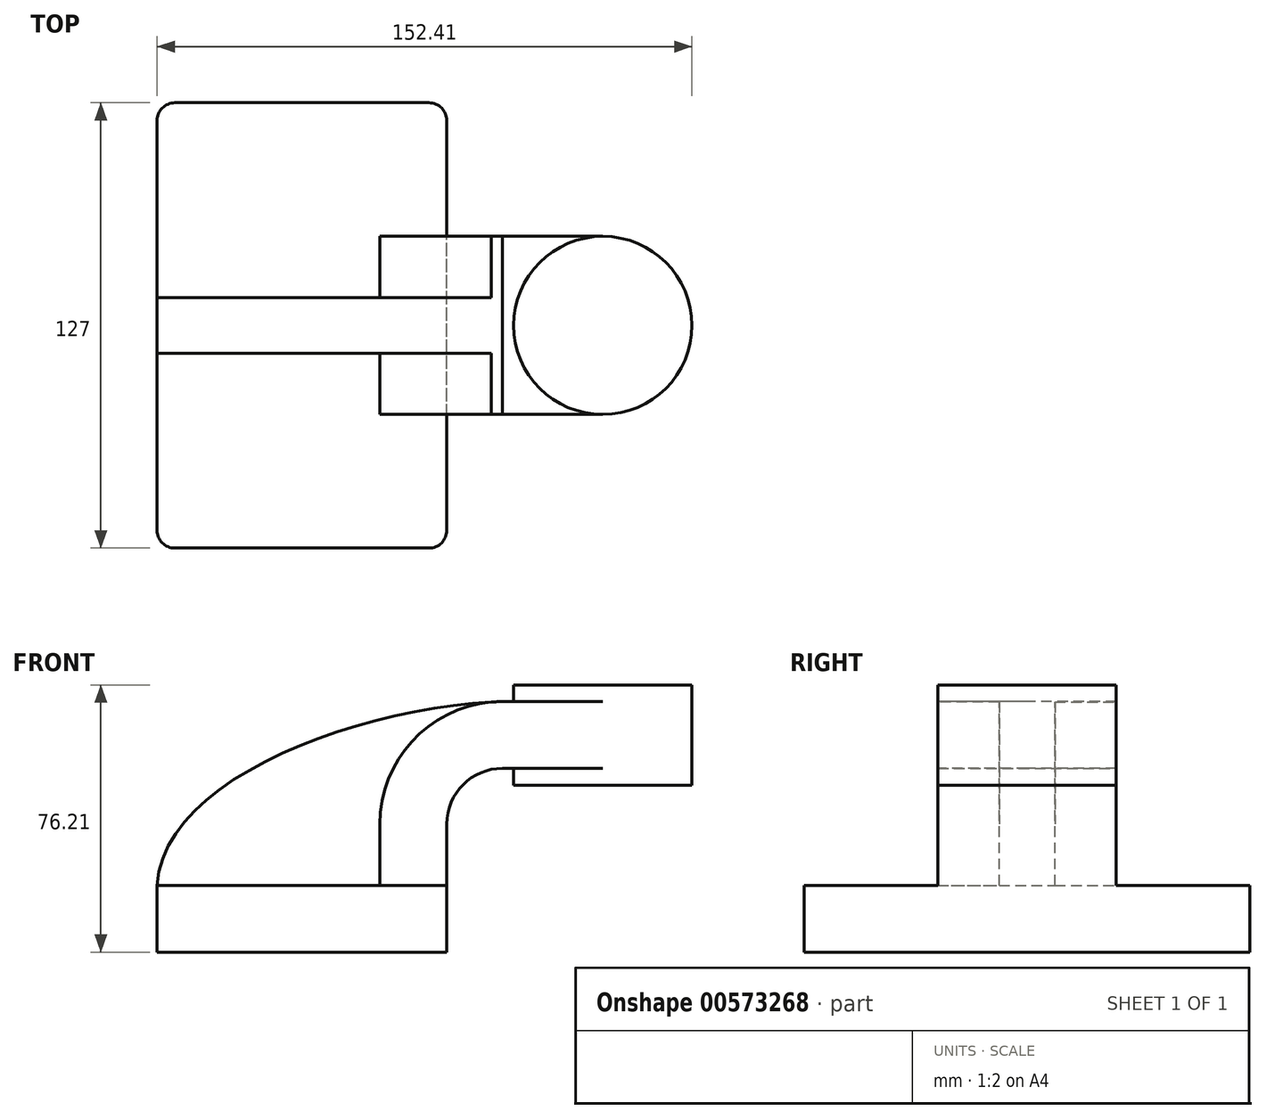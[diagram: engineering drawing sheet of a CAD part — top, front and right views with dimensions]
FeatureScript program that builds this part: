
annotation { "Feature Type Name" : "Feature", "Feature Type Description" : "" }
export const myFeature = defineFeature(function(context is Context, id is Id, definition is map)
    precondition{}
    {
        {
            var Q0;
            Q0=qCreatedBy(makeId("Front.planeOp"),FACE);
            var sketch = newSketch(context, id + "F0", { "sketchPlane" : qUnion([Q0])});
            skLineSegment(sketch, "E0.rect.bottom", {"start": v(-41.28, 9.52) * mm, "end": v(41.28, 9.52) * mm});
            skLineSegment(sketch, "E0.rect.top", {"start": v(-41.28, -9.52) * mm, "end": v(41.28, -9.52) * mm});
            skLineSegment(sketch, "E0.rect.left", {"start": v(-41.28, 9.52) * mm, "end": v(-41.28, -9.52) * mm});
            skLineSegment(sketch, "E0.rect.right", {"start": v(41.28, 9.52) * mm, "end": v(41.28, -9.52) * mm});
            skPoint(sketch, "E0.rect.middle", {"position": v(0, 0) * mm});
            skLineSegment(sketch, "E1", {"start": v(41.28, 9.52) * mm, "end": v(41.28, 27) * mm});
            skArc(sketch, "E2", {"start": v(41.28, 27) * mm, "mid": v(45.92, 38.23) * mm, "end": v(57.15, 42.88) * mm});
            skLineSegment(sketch, "E3", {"start": v(57.15, 42.88) * mm, "end": v(85.72, 42.88) * mm});
            skLineSegment(sketch, "E4.rect.bottom", {"start": v(60.32, 38.1) * mm, "end": v(111.12, 38.1) * mm});
            skLineSegment(sketch, "E4.rect.top", {"start": v(60.32, 66.68) * mm, "end": v(111.12, 66.68) * mm});
            skLineSegment(sketch, "E4.rect.left", {"start": v(60.32, 38.1) * mm, "end": v(60.32, 66.68) * mm});
            skLineSegment(sketch, "E4.rect.right", {"start": v(111.13, 38.1) * mm, "end": v(111.12, 66.68) * mm});
            skPoint(sketch, "E4.rect.middle", {"position": v(85.72, 52.39) * mm});
            skLineSegment(sketch, "E5.0", {"start": v(57.15, 61.93) * mm, "end": v(85.72, 61.93) * mm});
            skArc(sketch, "E5.1", {"start": v(22.23, 27) * mm, "mid": v(32.45, 51.7) * mm, "end": v(57.15, 61.93) * mm});
            skLineSegment(sketch, "E5.2", {"start": v(22.23, 9.52) * mm, "end": v(22.23, 27) * mm});
            skLineSegment(sketch, "E6", {"start": v(85.72, 38.1) * mm, "end": v(85.72, 66.68) * mm});
            skFitSpline(sketch, "E7", {"points": [v(-41.28, 9.53) * mm, v(57.15, 61.93) * mm], "startDerivative": vector(5.2, 92.34) * mm, "endDerivative": vector(120.92, 4.22) * mm});
            skSolve(sketch);
        }
        {
            var Q0;
            Q0=makeQuery(id+"F0.imprint","IMPRINT",FACE,{"disambiguationData":[TD([[makeQuery(id+"F0.imprint","IMPRINT",EDGE,{"derivedFrom":sQuery(id+"F0.wireOp",EDGE,"E0.rect.top")}),1.0]])]});
            extrude(context, id + "F1", {"entities" : qUnion([Q0]), "endBound" : BoundingType.SYMMETRIC, "depth" : 127 * mm});
        }
        {
            var Q0;
            {var subQ9=sQuery(id+"F0.wireOp",EDGE,"E1");Q0=makeQuery(id+"F0.imprint","IMPRINT",FACE,{"disambiguationData":[TD([[makeQuery(id+"F0.imprint","IMPRINT",EDGE,{"derivedFrom":subQ9}),1.0]])]});}
            var Q1;
            {var subQ0=sQuery(id+"F0.wireOp",EDGE,"E6");var subQ1=sQuery(id+"F0.wireOp",EDGE,"E3");var subQ2=makeQuery(id+"F0.imprint","INTERSECT",VERTEX,{"derivedFrom":[subQ1,subQ0]});Q1=makeQuery(id+"F0.imprint","IMPRINT",FACE,{"disambiguationData":[TD([[makeQuery(id+"F0.imprint","IMPRINT",EDGE,{"disambiguationData":[TD([[subQ2,1.0]])],"derivedFrom":subQ1}),1.0]])]});}
            extrude(context, id + "F2", {"entities" : qUnion([Q0, Q1]), "operationType" : NewBodyOperationType.ADD, "endBound" : BoundingType.SYMMETRIC, "depth" : 50.8 * mm});
        }
        {
            var Q0;
            {var subQ3=sQuery(id+"F0.wireOp",EDGE,"E5.2");Q0=makeQuery(id+"F0.imprint","IMPRINT",FACE,{"disambiguationData":[TD([[makeQuery(id+"F0.imprint","IMPRINT",EDGE,{"derivedFrom":subQ3}),1.0]])]});}
            extrude(context, id + "F3", {"entities" : qUnion([Q0]), "operationType" : NewBodyOperationType.ADD, "endBound" : BoundingType.SYMMETRIC, "depth" : 15.88 * mm});
        }
        {
            var Q0;
            {var subQ5=sQuery(id+"F0.wireOp",EDGE,"E4.rect.right");Q0=makeQuery(id+"F0.imprint","IMPRINT",FACE,{"disambiguationData":[TD([[makeQuery(id+"F0.imprint","IMPRINT",EDGE,{"derivedFrom":subQ5}),1.0]])]});}
            var Q1;
            Q1=sQuery(id+"F0.wireOp",EDGE,"E6");
            revolve(context, id + "F4", {"operationType" : NewBodyOperationType.ADD, "entities" : qUnion([Q0]), "axis" : qUnion([Q1]), "revolveType" : RevolveType.FULL});
        }
        {
            var Q0;
            Q0=makeQuery(id+"F1.opExtrude","CAP_EDGE",EDGE,{"disambiguationData":[OSD([sQuery(id+"F0.wireOp",EDGE,"E0.rect.right")])],"isStart":false});
            var Q1;
            Q1=makeQuery(id+"F1.opExtrude","CAP_EDGE",EDGE,{"disambiguationData":[OSD([sQuery(id+"F0.wireOp",EDGE,"E0.rect.left")])],"isStart":false});
            var Q2;
            Q2=makeQuery(id+"F1.opExtrude","CAP_EDGE",EDGE,{"disambiguationData":[OSD([sQuery(id+"F0.wireOp",EDGE,"E0.rect.right")])],"isStart":true});
            var Q3;
            Q3=makeQuery(id+"F1.opExtrude","CAP_EDGE",EDGE,{"disambiguationData":[OSD([sQuery(id+"F0.wireOp",EDGE,"E0.rect.left")])],"isStart":true});
            fillet(context, id + "F5", {"entities" : qUnion([Q0, Q1, Q2, Q3]), "radius" : 5.08 * mm, "tangentPropagation" : true, "allowEdgeOverflow" : false});
        }
        {
            var Q0;
            {var subQ4=sQuery(id+"F0.wireOp",EDGE,"E0.rect.bottom");var subQ5=sQuery(id+"F0.wireOp",EDGE,"E0.rect.right");var subQ6=sQuery(id+"F0.wireOp",EDGE,"E0.rect.left");Q0=makeQuery(id+"F3.boolean.opBoolean","SPLIT",FACE,{"disambiguationData":[TD([makeQuery(id+"F1.opExtrude","CAP_FACE",FACE,{"disambiguationData":[OSD([subQ4,sQuery(id+"F0.wireOp",EDGE,"E0.rect.top"),subQ6,subQ5])],"isStart":false})])],"derivedFrom":makeQuery(id+"F1.opExtrude","SWEPT_FACE",FACE,{"disambiguationData":[OSD([subQ4])]})});}
            var sketch = newSketch(context, id + "F6", { "sketchPlane" : qUnion([Q0])});
            skCircle(sketch, "E8", {"center": v(-84.5, -16.19) * mm, "radius": 15.7 * mm});
            skCircle(sketch, "E9", {"center": v(-3.73, -19.72) * mm, "radius": 12.7 * mm});
            skSolve(sketch);
        }
        {
            var Q0;
            Q0=sQuery(id+"F6.wireOp",EDGE,"E9");
            extrude(context, id + "F7", {"bodyType" : ToolBodyType.SURFACE, "surfaceEntities" : qUnion([Q0]), "oppositeDirection" : true, "depth" : 58.67 * mm, "offsetDistance" : 25.4 * mm});
        }
    });
